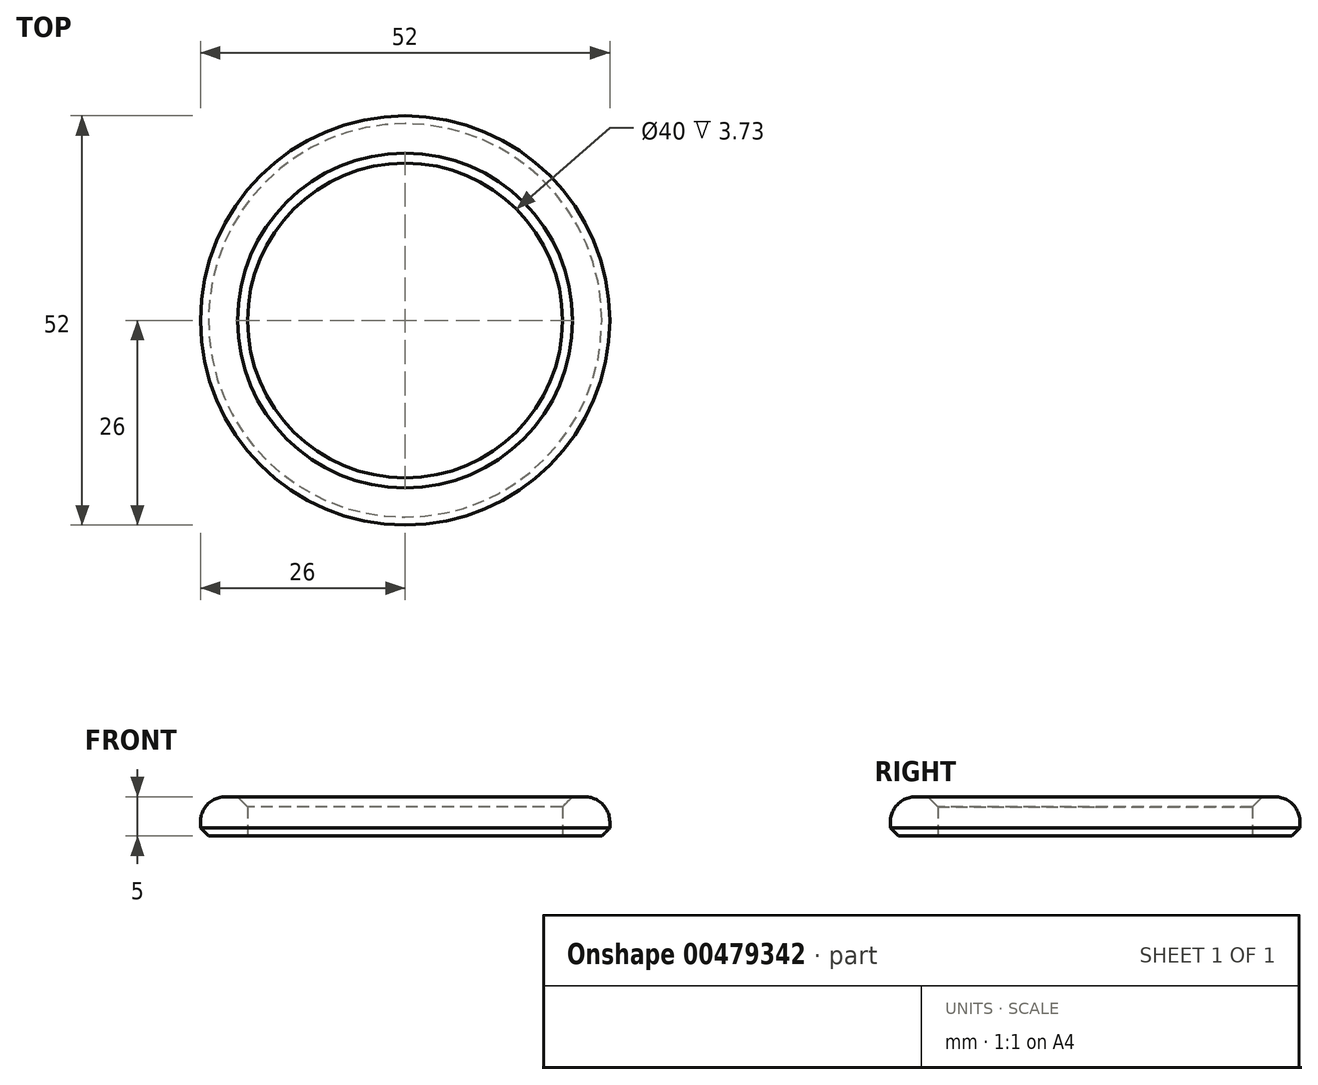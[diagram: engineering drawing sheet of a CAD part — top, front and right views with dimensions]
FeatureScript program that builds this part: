
annotation { "Feature Type Name" : "Feature", "Feature Type Description" : "" }
export const myFeature = defineFeature(function(context is Context, id is Id, definition is map)
    precondition{}
    {
        {
            var Q0;
            Q0=qCreatedBy(makeId("Top.planeOp"),FACE);
            var sketch = newSketch(context, id + "F0", { "sketchPlane" : qUnion([Q0])});
            skCircle(sketch, "E0", {"center": v(0, 0) * mm, "radius": 26 * mm});
            skCircle(sketch, "E1", {"center": v(0, 0) * mm, "radius": 20 * mm});
            skCircle(sketch, "E2", {"center": v(0, 0) * mm, "radius": 23 * mm});
            skSolve(sketch);
        }
        {
            var Q0;
            Q0=makeQuery(id+"F0.imprint","IMPRINT",FACE,{"disambiguationData":[TD([[makeQuery(id+"F0.imprint","IMPRINT",EDGE,{"derivedFrom":sQuery(id+"F0.wireOp",EDGE,"E1")}),-1.0]])]});
            extrude(context, id + "F1", {"entities" : qUnion([Q0]), "depth" : 5 * mm, "offsetDistance" : 25.4 * mm});
        }
        {
            var Q0;
            Q0=makeQuery(id+"F0.imprint","IMPRINT",FACE,{"disambiguationData":[TD([[makeQuery(id+"F0.imprint","IMPRINT",EDGE,{"derivedFrom":sQuery(id+"F0.wireOp",EDGE,"E0")}),1.0]])]});
            extrude(context, id + "F2", {"entities" : qUnion([Q0]), "operationType" : NewBodyOperationType.ADD, "depth" : 5 * mm, "offsetDistance" : 25.4 * mm});
        }
        {
            var Q0;
            Q0=makeQuery(id+"F2.opExtrude","CAP_EDGE",EDGE,{"disambiguationData":[OSD([sQuery(id+"F0.wireOp",EDGE,"E0")])],"isStart":false});
            fillet(context, id + "F3", {"entities" : qUnion([Q0]), "radius" : 3.17 * mm, "tangentPropagation" : true, "allowEdgeOverflow" : false});
        }
        {
            var Q0;
            Q0=makeQuery(id+"F1.opExtrude","CAP_EDGE",EDGE,{"disambiguationData":[OSD([sQuery(id+"F0.wireOp",EDGE,"E1")])],"isStart":false});
            chamfer(context, id + "F4", {"entities" : qUnion([Q0]), "width" : 1.27 * mm, "tangentPropagation" : true});
        }
        {
            var Q0;
            Q0=makeQuery(id+"F2.opExtrude","CAP_EDGE",EDGE,{"disambiguationData":[OSD([sQuery(id+"F0.wireOp",EDGE,"E0")])],"isStart":true});
            chamfer(context, id + "F5", {"entities" : qUnion([Q0]), "width" : 1.02 * mm, "tangentPropagation" : true});
        }
    });
